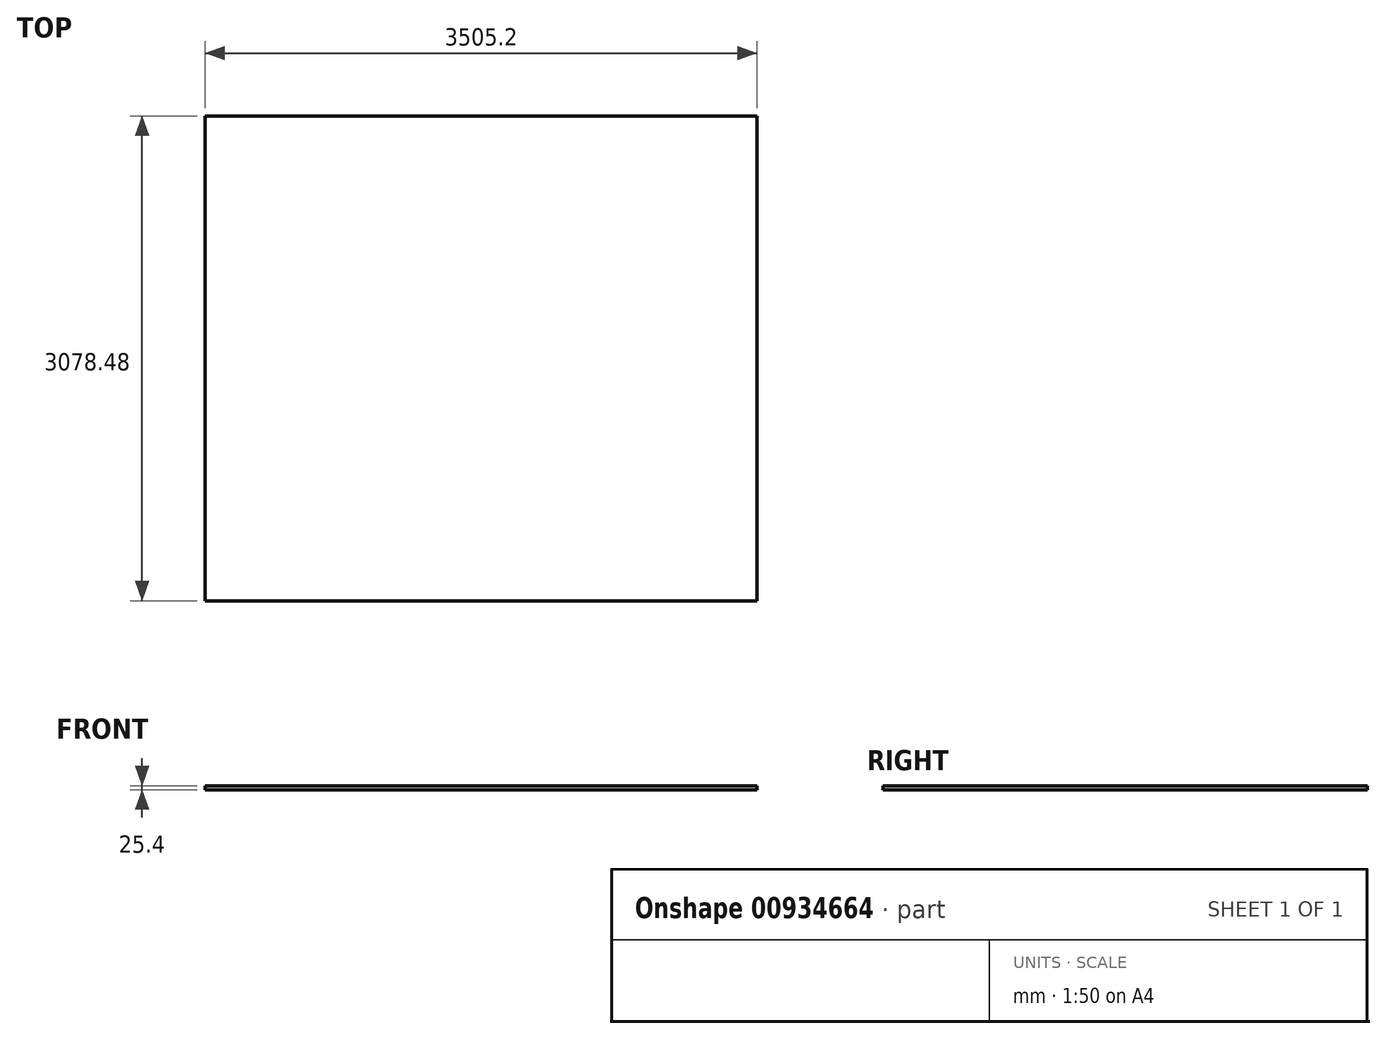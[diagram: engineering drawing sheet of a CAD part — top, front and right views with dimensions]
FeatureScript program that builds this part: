
annotation { "Feature Type Name" : "Feature", "Feature Type Description" : "" }
export const myFeature = defineFeature(function(context is Context, id is Id, definition is map)
    precondition{}
    {
        {
            var Q0;
            Q0=qCreatedBy(makeId("Top.planeOp"),FACE);
            var sketch = newSketch(context, id + "F0", { "sketchPlane" : qUnion([Q0])});
            skLineSegment(sketch, "E0.bottom", {"start": v(-3505.2, 0) * mm, "end": v(0, 0) * mm});
            skLineSegment(sketch, "E0.top", {"start": v(-3505.2, 3078.48) * mm, "end": v(0, 3078.48) * mm});
            skLineSegment(sketch, "E0.left", {"start": v(-3505.2, 0) * mm, "end": v(-3505.2, 3078.48) * mm});
            skLineSegment(sketch, "E0.right", {"start": v(0, 0) * mm, "end": v(0, 3078.48) * mm});
            skSolve(sketch);
        }
        {
            var Q0;
            Q0 = qSketchRegion(id + "F0", true);
            extrude(context, id + "F1", {"entities" : qUnion([Q0]), "depth" : 25.4 * mm, "offsetDistance" : 25.4 * mm});
        }
    });
